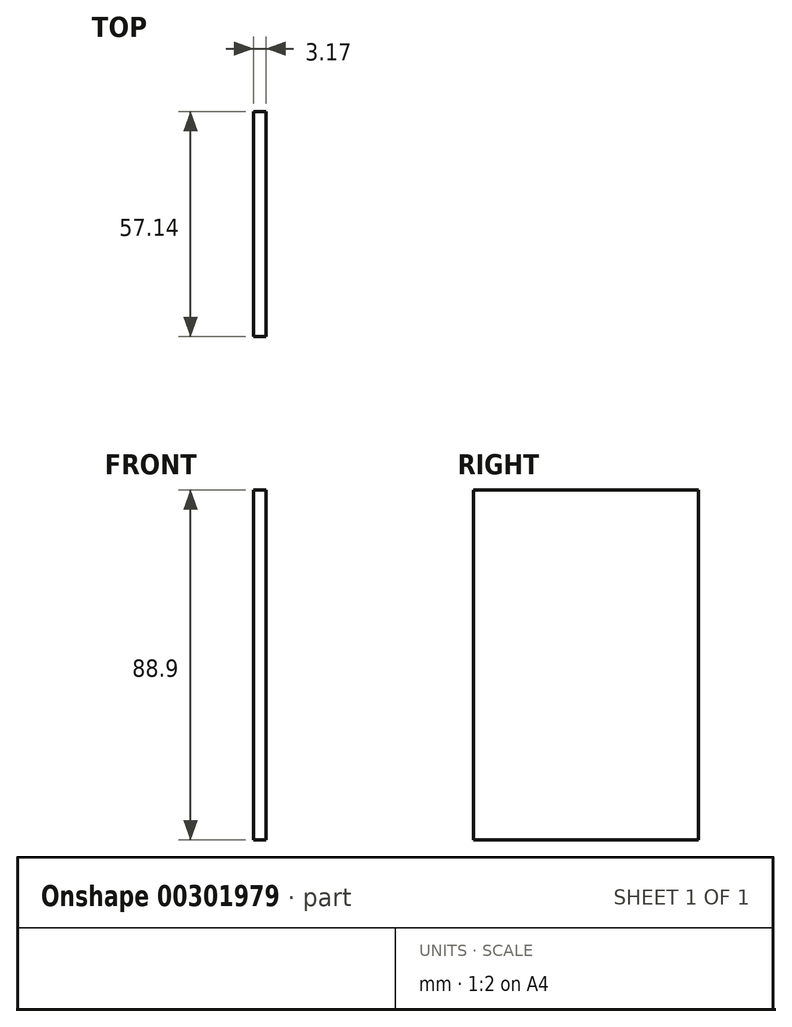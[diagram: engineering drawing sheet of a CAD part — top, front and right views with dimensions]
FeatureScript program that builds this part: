
annotation { "Feature Type Name" : "Feature", "Feature Type Description" : "" }
export const myFeature = defineFeature(function(context is Context, id is Id, definition is map)
    precondition{}
    {
        {
            var Q0;
            Q0=qCreatedBy(makeId("Right.planeOp"),FACE);
            var sketch = newSketch(context, id + "F0", { "sketchPlane" : qUnion([Q0])});
            skLineSegment(sketch, "E0.bottom", {"start": v(-28.57, 44.45) * mm, "end": v(28.58, 44.45) * mm});
            skLineSegment(sketch, "E0.top", {"start": v(-28.58, -44.45) * mm, "end": v(28.57, -44.45) * mm});
            skLineSegment(sketch, "E0.left", {"start": v(-28.57, 44.45) * mm, "end": v(-28.58, -44.45) * mm});
            skLineSegment(sketch, "E0.right", {"start": v(28.58, 44.45) * mm, "end": v(28.57, -44.45) * mm});
            skPoint(sketch, "E0.middle", {"position": v(0, 0) * mm});
            skSolve(sketch);
        }
        {
            var Q0;
            Q0=makeQuery(id+"F0.imprint","IMPRINT",FACE,{"disambiguationData":[TD([[makeQuery(id+"F0.imprint","IMPRINT",EDGE,{"derivedFrom":sQuery(id+"F0.wireOp",EDGE,"E0.bottom")}),-1.0]])]});
            extrude(context, id + "F1", {"entities" : qUnion([Q0]), "depth" : 3.17 * mm});
        }
    });
